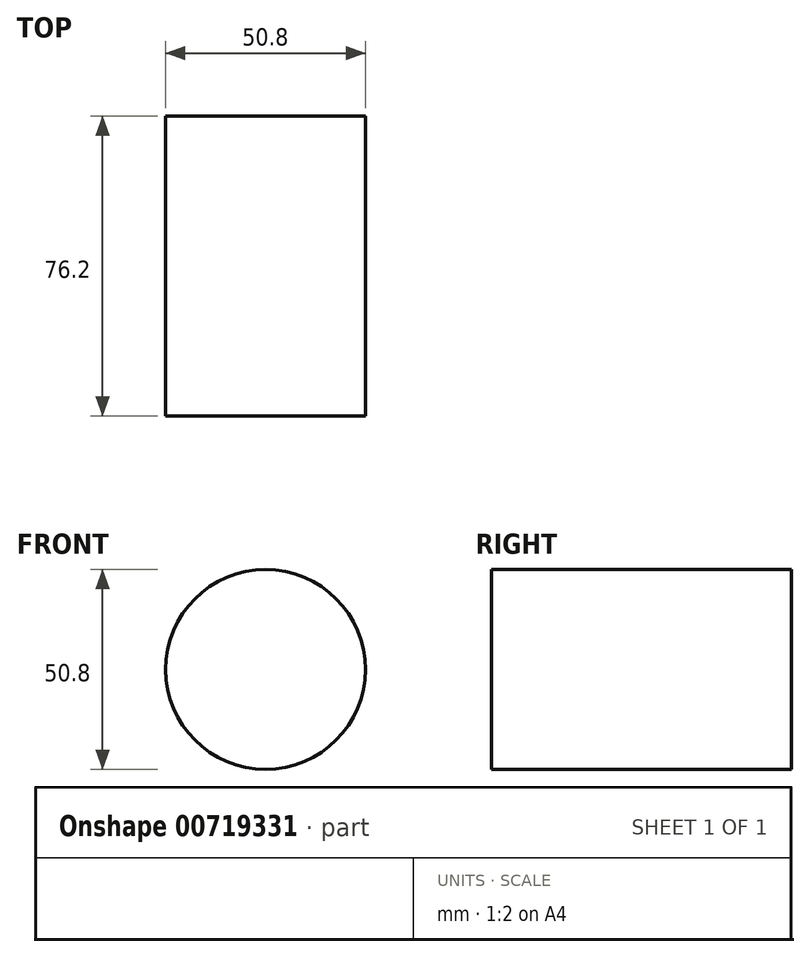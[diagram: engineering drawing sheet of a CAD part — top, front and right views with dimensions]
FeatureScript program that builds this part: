
annotation { "Feature Type Name" : "Feature", "Feature Type Description" : "" }
export const myFeature = defineFeature(function(context is Context, id is Id, definition is map)
    precondition{}
    {
        {
            var Q0;
            Q0=qCreatedBy(makeId("Front.planeOp"),FACE);
            var sketch = newSketch(context, id + "F0", { "sketchPlane" : qUnion([Q0])});
            skCircle(sketch, "E0", {"center": v(0, 0) * mm, "radius": 25.4 * mm});
            skSolve(sketch);
        }
        {
            var Q0;
            Q0 = qSketchRegion(id + "F0", true);
            extrude(context, id + "F1", {"entities" : qUnion([Q0]), "depth" : 76.2 * mm, "offsetDistance" : 25.4 * mm});
        }
    });
